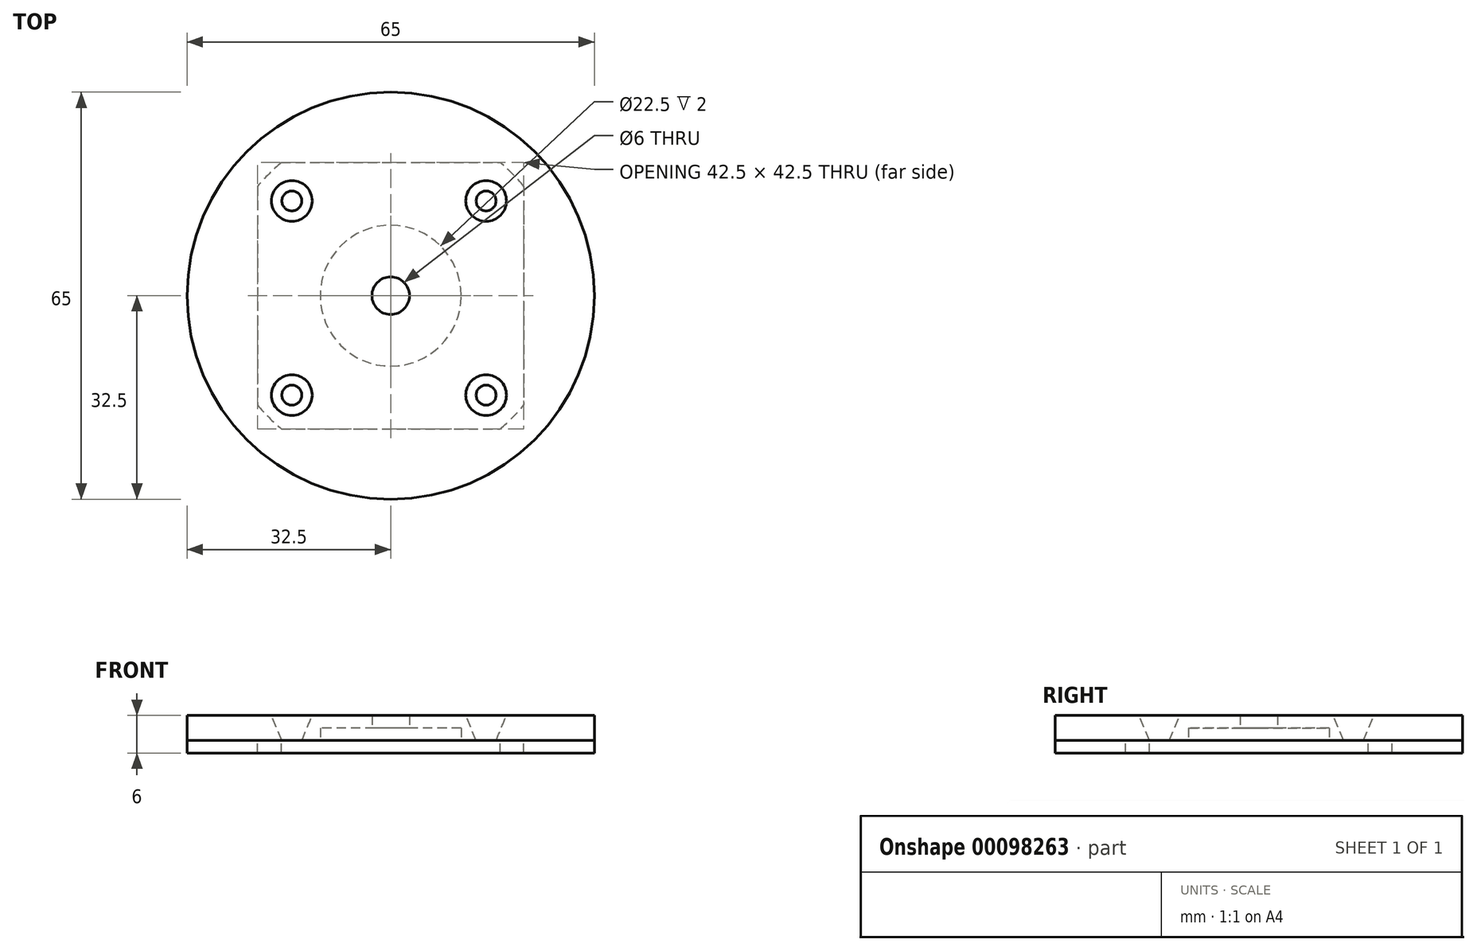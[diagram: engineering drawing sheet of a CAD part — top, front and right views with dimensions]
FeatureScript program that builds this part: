
annotation { "Feature Type Name" : "Feature", "Feature Type Description" : "" }
export const myFeature = defineFeature(function(context is Context, id is Id, definition is map)
    precondition{}
    {
        {
            var Q0;
            Q0=qCreatedBy(makeId("Top.planeOp"),FACE);
            var sketch = newSketch(context, id + "F0", { "sketchPlane" : qUnion([Q0])});
            skCircle(sketch, "E0", {"center": v(0, 0) * mm, "radius": 11.25 * mm});
            skLineSegment(sketch, "E1.bottom", {"start": v(-21.25, 21.25) * mm, "end": v(21.25, 21.25) * mm});
            skLineSegment(sketch, "E1.top", {"start": v(-21.25, -21.25) * mm, "end": v(21.25, -21.25) * mm});
            skLineSegment(sketch, "E1.left", {"start": v(-21.25, 21.25) * mm, "end": v(-21.25, -21.25) * mm});
            skLineSegment(sketch, "E1.right", {"start": v(21.25, 21.25) * mm, "end": v(21.25, -21.25) * mm});
            skLineSegment(sketch, "E2", {"start": v(-21.25, 21.25) * mm, "end": v(21.25, -21.25) * mm, "construction": true});
            skLineSegment(sketch, "E3", {"start": v(-21.25, -21.25) * mm, "end": v(21.25, 21.25) * mm, "construction": true});
            skPoint(sketch, "E4", {"position": v(-15.5, 15.5) * mm});
            skPoint(sketch, "E5.1.0", {"position": v(-15.5, -15.5) * mm});
            skPoint(sketch, "E5.2.0", {"position": v(15.5, -15.5) * mm});
            skPoint(sketch, "E5.3.0", {"position": v(15.5, 15.5) * mm});
            skPoint(sketch, "E6", {"position": v(-17.46, 21.25) * mm});
            skCircle(sketch, "E7", {"center": v(0, 0) * mm, "radius": 27.5 * mm});
            skCircle(sketch, "E8", {"center": v(0, 0) * mm, "radius": 25 * mm, "construction": true});
            skCircle(sketch, "E9", {"center": v(0, 0) * mm, "radius": 32.5 * mm});
            skSolve(sketch);
        }
        {
            var Q0;
            Q0=makeQuery(id+"F0.imprint","IMPRINT",FACE,{"disambiguationData":[TD([[makeQuery(id+"F0.imprint","IMPRINT",EDGE,{"derivedFrom":sQuery(id+"F0.wireOp",EDGE,"E9")}),1.0]])]});
            var Q1;
            {var subQ0=sQuery(id+"F0.wireOp",EDGE,"E1.left");var subQ1=sQuery(id+"F0.wireOp",EDGE,"E1.bottom");var subQ2=makeQuery(id+"F0.imprint","INTERSECT",VERTEX,{"derivedFrom":[subQ1,subQ0]});Q1=makeQuery(id+"F0.imprint","IMPRINT",FACE,{"disambiguationData":[TD([[makeQuery(id+"F0.imprint","IMPRINT",EDGE,{"disambiguationData":[TD([[subQ2,-1.0]])],"derivedFrom":subQ1}),-1.0]])]});}
            var Q2;
            {var subQ0=sQuery(id+"F0.wireOp",EDGE,"E1.right");var subQ1=sQuery(id+"F0.wireOp",EDGE,"E1.bottom");var subQ2=makeQuery(id+"F0.imprint","INTERSECT",VERTEX,{"derivedFrom":[subQ1,subQ0]});Q2=makeQuery(id+"F0.imprint","IMPRINT",FACE,{"disambiguationData":[TD([[makeQuery(id+"F0.imprint","IMPRINT",EDGE,{"disambiguationData":[TD([[subQ2,1.0]])],"derivedFrom":subQ1}),-1.0]])]});}
            var Q3;
            {var subQ0=sQuery(id+"F0.wireOp",EDGE,"E1.right");var subQ1=sQuery(id+"F0.wireOp",EDGE,"E1.top");var subQ2=makeQuery(id+"F0.imprint","INTERSECT",VERTEX,{"derivedFrom":[subQ1,subQ0]});Q3=makeQuery(id+"F0.imprint","IMPRINT",FACE,{"disambiguationData":[TD([[makeQuery(id+"F0.imprint","IMPRINT",EDGE,{"disambiguationData":[TD([[subQ2,1.0]])],"derivedFrom":subQ1}),1.0]])]});}
            var Q4;
            {var subQ0=sQuery(id+"F0.wireOp",EDGE,"E1.left");var subQ1=sQuery(id+"F0.wireOp",EDGE,"E1.top");var subQ2=makeQuery(id+"F0.imprint","INTERSECT",VERTEX,{"derivedFrom":[subQ1,subQ0]});Q4=makeQuery(id+"F0.imprint","IMPRINT",FACE,{"disambiguationData":[TD([[makeQuery(id+"F0.imprint","IMPRINT",EDGE,{"disambiguationData":[TD([[subQ2,-1.0]])],"derivedFrom":subQ1}),1.0]])]});}
            var Q5;
            {var subQ0=sQuery(id+"F0.wireOp",EDGE,"E7");var subQ1=sQuery(id+"F0.wireOp",EDGE,"E1.top");var subQ2=makeQuery(id+"F0.imprint","INTERSECT",VERTEX,{"disambiguationData":[OD(0.0)],"derivedFrom":[subQ1,subQ0]});Q5=makeQuery(id+"F0.imprint","IMPRINT",FACE,{"disambiguationData":[TD([[makeQuery(id+"F0.imprint","IMPRINT",EDGE,{"disambiguationData":[TD([[subQ2,-1.0]])],"derivedFrom":subQ1}),-1.0]])]});}
            var Q6;
            {var subQ0=sQuery(id+"F0.wireOp",EDGE,"E7");var subQ1=sQuery(id+"F0.wireOp",EDGE,"E1.right");var subQ2=makeQuery(id+"F0.imprint","INTERSECT",VERTEX,{"disambiguationData":[OD(0.0)],"derivedFrom":[subQ1,subQ0]});Q6=makeQuery(id+"F0.imprint","IMPRINT",FACE,{"disambiguationData":[TD([[makeQuery(id+"F0.imprint","IMPRINT",EDGE,{"disambiguationData":[TD([[subQ2,-1.0]])],"derivedFrom":subQ1}),1.0]])]});}
            var Q7;
            {var subQ0=sQuery(id+"F0.wireOp",EDGE,"E7");var subQ1=sQuery(id+"F0.wireOp",EDGE,"E1.bottom");var subQ2=makeQuery(id+"F0.imprint","INTERSECT",VERTEX,{"disambiguationData":[OD(0.0)],"derivedFrom":[subQ1,subQ0]});Q7=makeQuery(id+"F0.imprint","IMPRINT",FACE,{"disambiguationData":[TD([[makeQuery(id+"F0.imprint","IMPRINT",EDGE,{"disambiguationData":[TD([[subQ2,-1.0]])],"derivedFrom":subQ1}),1.0]])]});}
            var Q8;
            {var subQ0=sQuery(id+"F0.wireOp",EDGE,"E7");var subQ1=sQuery(id+"F0.wireOp",EDGE,"E1.left");var subQ2=makeQuery(id+"F0.imprint","INTERSECT",VERTEX,{"disambiguationData":[OD(0.0)],"derivedFrom":[subQ1,subQ0]});Q8=makeQuery(id+"F0.imprint","IMPRINT",FACE,{"disambiguationData":[TD([[makeQuery(id+"F0.imprint","IMPRINT",EDGE,{"disambiguationData":[TD([[subQ2,-1.0]])],"derivedFrom":subQ1}),-1.0]])]});}
            var Q9;
            Q9=makeQuery(id+"F0.imprint","IMPRINT",FACE,{"disambiguationData":[TD([[makeQuery(id+"F0.imprint","IMPRINT",EDGE,{"derivedFrom":sQuery(id+"F0.wireOp",EDGE,"E0")}),-1.0]])]});
            extrude(context, id + "F1", {"entities" : qUnion([Q0, Q1, Q2, Q3, Q4, Q5, Q6, Q7, Q8, Q9]), "depth" : 2 * mm});
        }
        {
            var Q0;
            {var subQ0=sQuery(id+"F0.wireOp",EDGE,"E7");var subQ1=sQuery(id+"F0.wireOp",EDGE,"E1.left");var subQ2=makeQuery(id+"F0.imprint","INTERSECT",VERTEX,{"disambiguationData":[OD(0.0)],"derivedFrom":[subQ1,subQ0]});Q0=makeQuery(id+"F0.imprint","IMPRINT",FACE,{"disambiguationData":[TD([[makeQuery(id+"F0.imprint","IMPRINT",EDGE,{"disambiguationData":[TD([[subQ2,-1.0]])],"derivedFrom":subQ1}),-1.0]])]});}
            var Q1;
            Q1=makeQuery(id+"F0.imprint","IMPRINT",FACE,{"disambiguationData":[TD([[makeQuery(id+"F0.imprint","IMPRINT",EDGE,{"derivedFrom":sQuery(id+"F0.wireOp",EDGE,"E9")}),1.0]])]});
            var Q2;
            {var subQ0=sQuery(id+"F0.wireOp",EDGE,"E1.left");var subQ1=sQuery(id+"F0.wireOp",EDGE,"E1.top");var subQ2=makeQuery(id+"F0.imprint","INTERSECT",VERTEX,{"derivedFrom":[subQ1,subQ0]});Q2=makeQuery(id+"F0.imprint","IMPRINT",FACE,{"disambiguationData":[TD([[makeQuery(id+"F0.imprint","IMPRINT",EDGE,{"disambiguationData":[TD([[subQ2,-1.0]])],"derivedFrom":subQ1}),1.0]])]});}
            var Q3;
            {var subQ0=sQuery(id+"F0.wireOp",EDGE,"E7");var subQ1=sQuery(id+"F0.wireOp",EDGE,"E1.top");var subQ2=makeQuery(id+"F0.imprint","INTERSECT",VERTEX,{"disambiguationData":[OD(0.0)],"derivedFrom":[subQ1,subQ0]});Q3=makeQuery(id+"F0.imprint","IMPRINT",FACE,{"disambiguationData":[TD([[makeQuery(id+"F0.imprint","IMPRINT",EDGE,{"disambiguationData":[TD([[subQ2,-1.0]])],"derivedFrom":subQ1}),-1.0]])]});}
            var Q4;
            {var subQ0=sQuery(id+"F0.wireOp",EDGE,"E1.right");var subQ1=sQuery(id+"F0.wireOp",EDGE,"E1.top");var subQ2=makeQuery(id+"F0.imprint","INTERSECT",VERTEX,{"derivedFrom":[subQ1,subQ0]});Q4=makeQuery(id+"F0.imprint","IMPRINT",FACE,{"disambiguationData":[TD([[makeQuery(id+"F0.imprint","IMPRINT",EDGE,{"disambiguationData":[TD([[subQ2,1.0]])],"derivedFrom":subQ1}),1.0]])]});}
            var Q5;
            {var subQ0=sQuery(id+"F0.wireOp",EDGE,"E1.right");var subQ1=sQuery(id+"F0.wireOp",EDGE,"E1.bottom");var subQ2=makeQuery(id+"F0.imprint","INTERSECT",VERTEX,{"derivedFrom":[subQ1,subQ0]});Q5=makeQuery(id+"F0.imprint","IMPRINT",FACE,{"disambiguationData":[TD([[makeQuery(id+"F0.imprint","IMPRINT",EDGE,{"disambiguationData":[TD([[subQ2,1.0]])],"derivedFrom":subQ1}),-1.0]])]});}
            var Q6;
            {var subQ0=sQuery(id+"F0.wireOp",EDGE,"E7");var subQ1=sQuery(id+"F0.wireOp",EDGE,"E1.right");var subQ2=makeQuery(id+"F0.imprint","INTERSECT",VERTEX,{"disambiguationData":[OD(0.0)],"derivedFrom":[subQ1,subQ0]});Q6=makeQuery(id+"F0.imprint","IMPRINT",FACE,{"disambiguationData":[TD([[makeQuery(id+"F0.imprint","IMPRINT",EDGE,{"disambiguationData":[TD([[subQ2,-1.0]])],"derivedFrom":subQ1}),1.0]])]});}
            var Q7;
            {var subQ0=sQuery(id+"F0.wireOp",EDGE,"E7");var subQ1=sQuery(id+"F0.wireOp",EDGE,"E1.bottom");var subQ2=makeQuery(id+"F0.imprint","INTERSECT",VERTEX,{"disambiguationData":[OD(0.0)],"derivedFrom":[subQ1,subQ0]});Q7=makeQuery(id+"F0.imprint","IMPRINT",FACE,{"disambiguationData":[TD([[makeQuery(id+"F0.imprint","IMPRINT",EDGE,{"disambiguationData":[TD([[subQ2,-1.0]])],"derivedFrom":subQ1}),1.0]])]});}
            var Q8;
            {var subQ0=sQuery(id+"F0.wireOp",EDGE,"E1.left");var subQ1=sQuery(id+"F0.wireOp",EDGE,"E1.bottom");var subQ2=makeQuery(id+"F0.imprint","INTERSECT",VERTEX,{"derivedFrom":[subQ1,subQ0]});Q8=makeQuery(id+"F0.imprint","IMPRINT",FACE,{"disambiguationData":[TD([[makeQuery(id+"F0.imprint","IMPRINT",EDGE,{"disambiguationData":[TD([[subQ2,-1.0]])],"derivedFrom":subQ1}),-1.0]])]});}
            extrude(context, id + "F2", {"entities" : qUnion([Q0, Q1, Q2, Q3, Q4, Q5, Q6, Q7, Q8]), "oppositeDirection" : true, "depth" : 2 * mm});
        }
        {
            var Q0;
            Q0=makeQuery(id+"F1.opExtrude","CAP_FACE",FACE,{"disambiguationData":[OSD([sQuery(id+"F0.wireOp",EDGE,"E0"),sQuery(id+"F0.wireOp",EDGE,"E9")])],"isStart":false});
            var sketch = newSketch(context, id + "F3", { "sketchPlane" : qUnion([Q0])});
            skCircle(sketch, "E10", {"center": v(0, 0) * mm, "radius": 3 * mm});
            skPoint(sketch, "E11", {"position": v(15.5, -15.5) * mm});
            skPoint(sketch, "E12", {"position": v(-15.5, -15.5) * mm});
            skPoint(sketch, "E13", {"position": v(-15.5, 15.5) * mm});
            skPoint(sketch, "E14.3.0", {"position": v(15.5, 15.5) * mm});
            skLineSegment(sketch, "E15", {"start": v(-15.5, -15.5) * mm, "end": v(15.5, 15.5) * mm});
            skLineSegment(sketch, "E16", {"start": v(-15.5, 15.5) * mm, "end": v(15.5, -15.5) * mm});
            skSolve(sketch);
        }
        {
            var Q0;
            {var subQ1=sQuery(id+"F0.wireOp",EDGE,"E0");Q0=makeQuery(id+"F3.imprint","IMPRINT",FACE,{"disambiguationData":[TD([[makeQuery(id+"F3.imprint","IMPRINT",EDGE,{"derivedFrom":makeQuery(id+"F1.opExtrude","CAP_EDGE",EDGE,{"disambiguationData":[OSD([subQ1])],"isStart":false})}),-1.0]])]});}
            var Q1;
            Q1=makeQuery(id+"F3.imprint","IMPRINT",FACE,{"disambiguationData":[TD([[makeQuery(id+"F3.imprint","IMPRINT",EDGE,{"derivedFrom":sQuery(id+"F3.wireOp",EDGE,"E10")}),-1.0]])]});
            extrude(context, id + "F4", {"entities" : qUnion([Q0, Q1]), "operationType" : NewBodyOperationType.ADD, "depth" : 2 * mm});
        }
        {
            var Q0;
            Q0=makeQuery(id+"F4.opExtrude","CAP_FACE",FACE,{"disambiguationData":[OSD([sQuery(id+"F0.wireOp",EDGE,"E9"),sQuery(id+"F3.wireOp",EDGE,"E10")])],"isStart":false});
            var sketch = newSketch(context, id + "F5", { "sketchPlane" : qUnion([Q0])});
            skPoint(sketch, "E17", {"position": v(-15.77, 15.13) * mm});
            skPoint(sketch, "E18.1.0", {"position": v(-15.77, -15.87) * mm});
            skPoint(sketch, "E18.2.0", {"position": v(15.23, -15.87) * mm});
            skPoint(sketch, "E18.3.0", {"position": v(15.23, 15.13) * mm});
            skSolve(sketch);
        }
        {
            var Q0;
            Q0=sQuery(id+"F5.wireOp",VERTEX,"E17");
            var Q1;
            Q1=sQuery(id+"F5.wireOp",VERTEX,"E18.1.0");
            var Q2;
            Q2=sQuery(id+"F5.wireOp",VERTEX,"E18.2.0");
            var Q3;
            Q3=sQuery(id+"F5.wireOp",VERTEX,"E18.3.0");
            var Q4;
            Q4=makeQuery(id+"F1.opExtrude","SWEPT_BODY",BODY,{"disambiguationData":[OSD([sQuery(id+"F0.wireOp",EDGE,"E0"),sQuery(id+"F0.wireOp",EDGE,"E9")])]});
            hole(context, id + "F6", {"style" : HoleStyle.C_SINK, "endStyle" : HoleEndStyle.BLIND, "holeDiameter" : 3 * mm, "cSinkDiameter" : 6.5 * mm, "cSinkAngle" : 45 * degree, "holeDepth" : 12 * mm, "locations" : qUnion([Q0, Q1, Q2, Q3]), "scope" : qUnion([Q4])});
        }
    });
